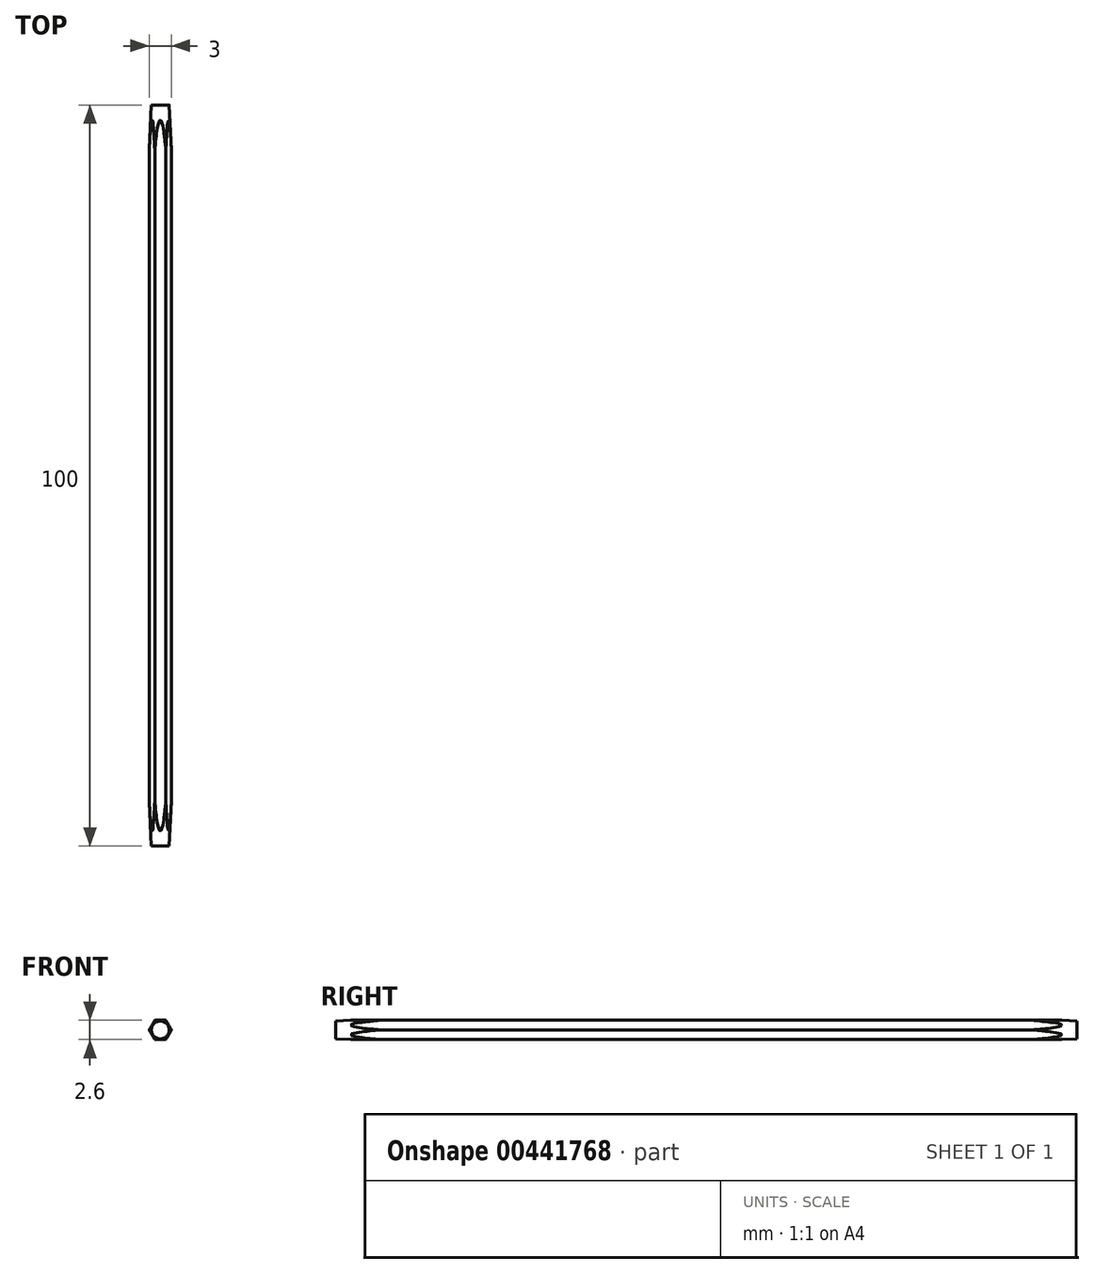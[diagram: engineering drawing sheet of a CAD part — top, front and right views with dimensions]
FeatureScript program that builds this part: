
annotation { "Feature Type Name" : "Feature", "Feature Type Description" : "" }
export const myFeature = defineFeature(function(context is Context, id is Id, definition is map)
    precondition{}
    {
        {
            var Q0;
            Q0=qCreatedBy(makeId("Front.planeOp"),FACE);
            var sketch = newSketch(context, id + "F0", { "sketchPlane" : qUnion([Q0])});
            skCircle(sketch, "E0.cCircle", {"center": v(0, 0) * mm, "radius": 1.5 * mm, "construction": true});
            skLineSegment(sketch, "E0.0", {"start": v(-1.5, 0) * mm, "end": v(-0.75, 1.3) * mm});
            skLineSegment(sketch, "E0.1", {"start": v(-0.75, 1.3) * mm, "end": v(0.75, 1.3) * mm});
            skLineSegment(sketch, "E0.2", {"start": v(0.75, 1.3) * mm, "end": v(1.5, 0) * mm});
            skLineSegment(sketch, "E0.3", {"start": v(1.5, 0) * mm, "end": v(0.75, -1.3) * mm});
            skLineSegment(sketch, "E0.4", {"start": v(0.75, -1.3) * mm, "end": v(-0.75, -1.3) * mm});
            skLineSegment(sketch, "E0.5", {"start": v(-0.75, -1.3) * mm, "end": v(-1.5, 0) * mm});
            skSolve(sketch);
        }
        {
            var Q0;
            Q0 = qSketchRegion(id + "F0", true);
            extrude(context, id + "F1", {"entities" : qUnion([Q0]), "depth" : 50 * mm});
        }
        {
            var Q0;
            Q0=qCreatedBy(makeId("Right.planeOp"),FACE);
            var sketch = newSketch(context, id + "F2", { "sketchPlane" : qUnion([Q0])});
            skLineSegment(sketch, "E1", {"start": v(-50, 1.2) * mm, "end": v(-48, 1.3) * mm});
            skLineSegment(sketch, "E2", {"start": v(0, 0) * mm, "end": v(15.07, 0) * mm});
            skLineSegment(sketch, "E3", {"start": v(-48, 1.3) * mm, "end": v(-36.08, 1.89) * mm});
            skLineSegment(sketch, "E4", {"start": v(-36.08, 1.89) * mm, "end": v(-51.04, 1.89) * mm});
            skLineSegment(sketch, "E5", {"start": v(-51.04, 1.89) * mm, "end": v(-51.04, 1.15) * mm});
            skLineSegment(sketch, "E6", {"start": v(-51.04, 1.15) * mm, "end": v(-50, 1.2) * mm});
            skSolve(sketch);
        }
        {
            var Q0;
            Q0=makeQuery(id+"F2.imprint","IMPRINT",FACE,{"disambiguationData":[TD([[makeQuery(id+"F2.imprint","IMPRINT",EDGE,{"derivedFrom":sQuery(id+"F2.wireOp",EDGE,"E1")}),1.0]])]});
            var Q1;
            Q1=sQuery(id+"F2.wireOp",EDGE,"E2");
            revolve(context, id + "F3", {"operationType" : NewBodyOperationType.REMOVE, "entities" : qUnion([Q0]), "axis" : qUnion([Q1]), "revolveType" : RevolveType.FULL, "oppositeDirection" : true});
        }
        {
            var Q0;
            Q0=makeQuery(id+"F1.opExtrude","SWEPT_BODY",BODY,{"disambiguationData":[OSD([sQuery(id+"F0.wireOp",EDGE,"E0.0"),sQuery(id+"F0.wireOp",EDGE,"E0.1"),sQuery(id+"F0.wireOp",EDGE,"E0.2"),sQuery(id+"F0.wireOp",EDGE,"E0.3"),sQuery(id+"F0.wireOp",EDGE,"E0.4"),sQuery(id+"F0.wireOp",EDGE,"E0.5")])]});
            var Q1;
            Q1=qCreatedBy(makeId("Front.planeOp"),FACE);
            mirror(context, id + "F4", {"operationType" : NewBodyOperationType.ADD, "entities" : qUnion([Q0]), "mirrorPlane" : qUnion([Q1])});
        }
    });
